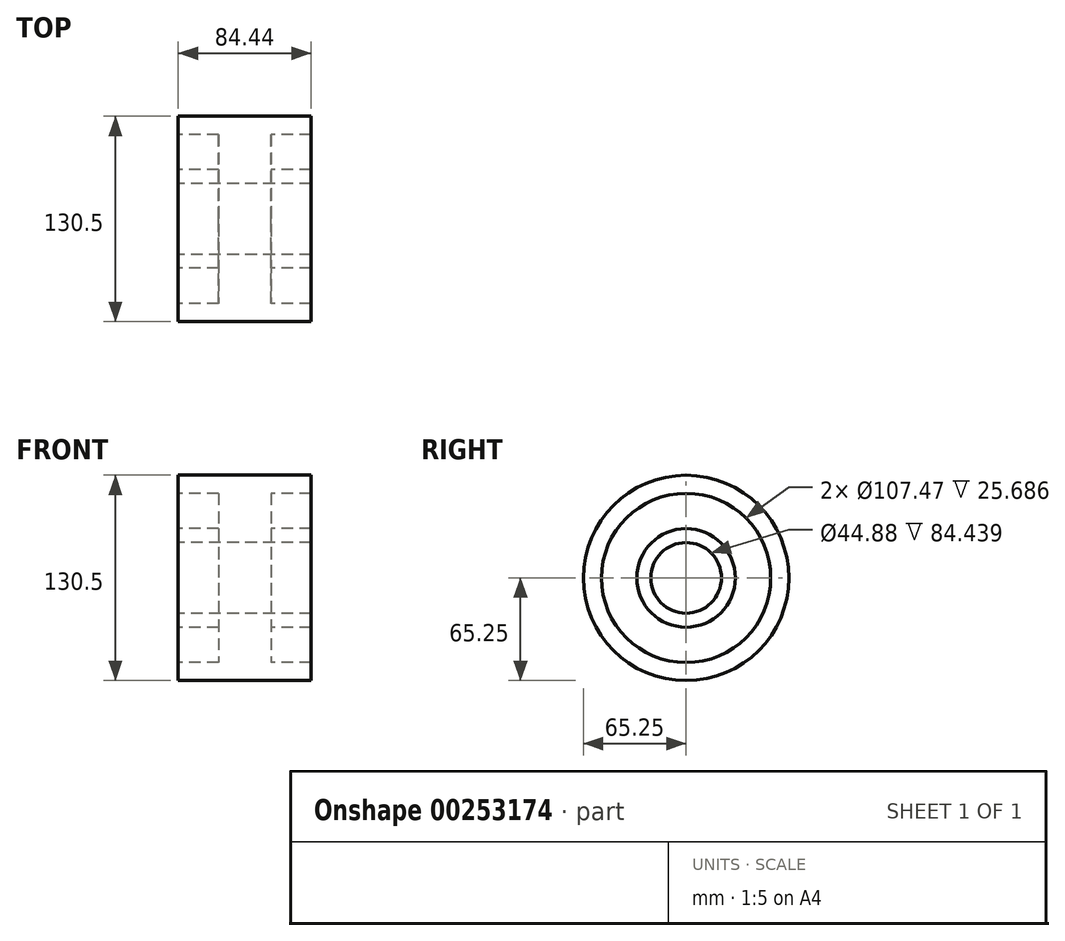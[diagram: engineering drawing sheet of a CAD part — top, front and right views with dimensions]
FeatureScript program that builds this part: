
annotation { "Feature Type Name" : "Feature", "Feature Type Description" : "" }
export const myFeature = defineFeature(function(context is Context, id is Id, definition is map)
    precondition{}
    {
        {
            var Q0;
            Q0=qCreatedBy(makeId("Front.planeOp"),FACE);
            var sketch = newSketch(context, id + "F0", { "sketchPlane" : qUnion([Q0])});
            skLineSegment(sketch, "E0", {"start": v(-76.47, 0) * mm, "end": v(81.78, 0) * mm, "construction": true});
            skLineSegment(sketch, "E1", {"start": v(0, 73.22) * mm, "end": v(0, 0) * mm, "construction": true});
            skLineSegment(sketch, "E2", {"start": v(0, 65.25) * mm, "end": v(42.22, 65.25) * mm});
            skLineSegment(sketch, "E3", {"start": v(42.22, 65.25) * mm, "end": v(42.22, 53.73) * mm});
            skLineSegment(sketch, "E4", {"start": v(42.22, 53.73) * mm, "end": v(16.53, 53.73) * mm});
            skLineSegment(sketch, "E5", {"start": v(16.53, 53.73) * mm, "end": v(16.53, 31.3) * mm});
            skLineSegment(sketch, "E6", {"start": v(16.53, 31.3) * mm, "end": v(42.22, 31.3) * mm});
            skLineSegment(sketch, "E7", {"start": v(42.22, 31.3) * mm, "end": v(42.22, 22.44) * mm});
            skLineSegment(sketch, "E8", {"start": v(42.22, 22.44) * mm, "end": v(0, 22.44) * mm});
            skLineSegment(sketch, "E9.MirrorCS", {"start": v(0, 65.25) * mm, "end": v(-42.22, 65.25) * mm});
            skLineSegment(sketch, "E10.MirrorCS", {"start": v(-42.22, 65.25) * mm, "end": v(-42.22, 53.73) * mm});
            skLineSegment(sketch, "E11.MirrorCS", {"start": v(-42.22, 53.73) * mm, "end": v(-16.53, 53.73) * mm});
            skLineSegment(sketch, "E12.MirrorCS", {"start": v(-16.53, 53.73) * mm, "end": v(-16.53, 31.3) * mm});
            skLineSegment(sketch, "E13.MirrorCS", {"start": v(-16.53, 31.3) * mm, "end": v(-42.22, 31.3) * mm});
            skLineSegment(sketch, "E14.MirrorCS", {"start": v(-42.22, 31.3) * mm, "end": v(-42.22, 22.44) * mm});
            skLineSegment(sketch, "E15.MirrorCS", {"start": v(-42.22, 22.44) * mm, "end": v(0, 22.44) * mm});
            skSolve(sketch);
        }
        {
            var Q0;
            Q0 = qSketchRegion(id + "F0", true);
            var Q1;
            Q1=sQuery(id+"F0.wireOp",EDGE,"E0");
            revolve(context, id + "F1", {"entities" : qUnion([Q0]), "axis" : qUnion([Q1]), "revolveType" : RevolveType.FULL});
        }
    });
